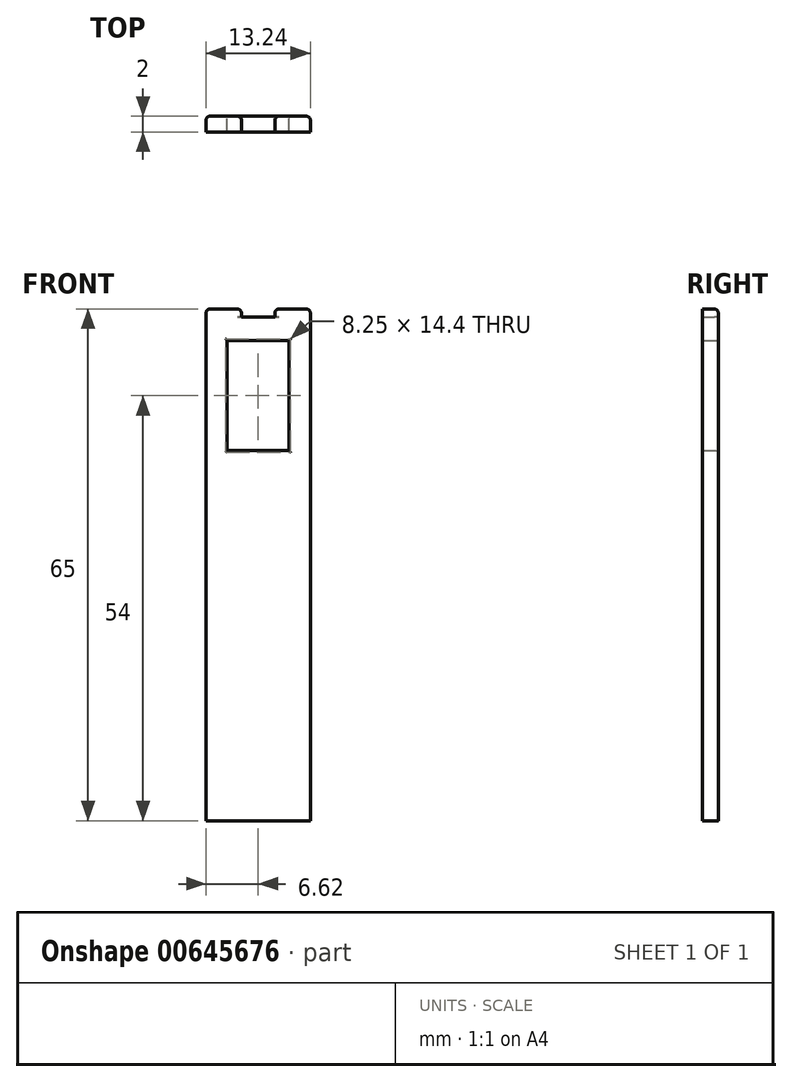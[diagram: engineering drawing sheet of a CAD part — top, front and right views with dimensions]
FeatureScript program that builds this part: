
annotation { "Feature Type Name" : "Feature", "Feature Type Description" : "" }
export const myFeature = defineFeature(function(context is Context, id is Id, definition is map)
    precondition{}
    {
        {
            var Q0;
            Q0=qCreatedBy(makeId("Front.planeOp"),FACE);
            var sketch = newSketch(context, id + "F0", { "sketchPlane" : qUnion([Q0])});
            skLineSegment(sketch, "E0.bottom", {"start": v(-6.62, 32.5) * mm, "end": v(6.63, 32.5) * mm});
            skLineSegment(sketch, "E0.top", {"start": v(-6.63, -32.5) * mm, "end": v(6.62, -32.5) * mm});
            skLineSegment(sketch, "E0.left", {"start": v(-6.62, 32.5) * mm, "end": v(-6.63, -32.5) * mm});
            skLineSegment(sketch, "E0.right", {"start": v(6.63, 32.5) * mm, "end": v(6.62, -32.5) * mm});
            skPoint(sketch, "E0.middle", {"position": v(0, 0) * mm});
            skLineSegment(sketch, "E1.bottom", {"start": v(-3.92, 28.5) * mm, "end": v(3.93, 28.5) * mm});
            skLineSegment(sketch, "E1.top", {"start": v(-3.92, 14.5) * mm, "end": v(3.93, 14.5) * mm});
            skLineSegment(sketch, "E1.left", {"start": v(-3.92, 28.5) * mm, "end": v(-3.92, 14.5) * mm});
            skLineSegment(sketch, "E1.right", {"start": v(3.93, 28.5) * mm, "end": v(3.93, 14.5) * mm});
            skSolve(sketch);
        }
        {
            var Q0;
            Q0=makeQuery(id+"F0.imprint","IMPRINT",FACE,{"disambiguationData":[TD([[makeQuery(id+"F0.imprint","IMPRINT",EDGE,{"derivedFrom":sQuery(id+"F0.wireOp",EDGE,"E0.bottom")}),-1.0]])]});
            extrude(context, id + "F1", {"entities" : qUnion([Q0]), "depth" : 2 * mm, "offsetDistance" : 25 * mm});
        }
        {
            var Q0;
            Q0=sQuery(id+"F0.wireOp",EDGE,"E1.left");
            var Q1;
            Q1=sQuery(id+"F0.wireOp",EDGE,"E1.bottom");
            var Q2;
            Q2=sQuery(id+"F0.wireOp",EDGE,"E1.right");
            var Q3;
            Q3=sQuery(id+"F0.wireOp",EDGE,"E1.top");
            extrude(context, id + "F2", {"bodyType" : ToolBodyType.SURFACE, "surfaceEntities" : qUnion([Q0, Q1, Q2, Q3]), "depth" : 2 * mm, "offsetDistance" : 25 * mm});
        }
        {
            var Q0;
            Q0=qCreatedBy(makeId("Front.planeOp"),FACE);
            var sketch = newSketch(context, id + "F3", { "sketchPlane" : qUnion([Q0])});
            skLineSegment(sketch, "E2.bottom", {"start": v(-2.13, 33.67) * mm, "end": v(2.12, 33.67) * mm});
            skLineSegment(sketch, "E2.top", {"start": v(-2.13, 31.5) * mm, "end": v(2.12, 31.5) * mm});
            skLineSegment(sketch, "E2.left", {"start": v(-2.13, 33.67) * mm, "end": v(-2.13, 31.5) * mm});
            skLineSegment(sketch, "E2.right", {"start": v(2.12, 33.67) * mm, "end": v(2.12, 31.5) * mm});
            skPoint(sketch, "E2.middle", {"position": v(0, 32.58) * mm});
            skSolve(sketch);
        }
        {
            var Q0;
            Q0=makeQuery(id+"F3.imprint","IMPRINT",FACE,{"disambiguationData":[TD([[makeQuery(id+"F3.imprint","IMPRINT",EDGE,{"derivedFrom":sQuery(id+"F3.wireOp",EDGE,"E2.bottom")}),-1.0]])]});
            extrude(context, id + "F4", {"entities" : qUnion([Q0]), "operationType" : NewBodyOperationType.REMOVE, "depth" : 25 * mm, "offsetDistance" : 25 * mm});
        }
        {
            var Q0;
            Q0=makeQuery(id+"F4.boolean.opBoolean","INTERSECT",EDGE,{"derivedFrom":[makeQuery(id+"F1.opExtrude","SWEPT_FACE",FACE,{"disambiguationData":[OSD([sQuery(id+"F0.wireOp",EDGE,"E0.bottom")])]}),makeQuery(id+"F4.opExtrude","SWEPT_FACE",FACE,{"disambiguationData":[OSD([sQuery(id+"F3.wireOp",EDGE,"E2.left")])]})]});
            var Q1;
            Q1=makeQuery(id+"F1.opExtrude","SWEPT_EDGE",EDGE,{"disambiguationData":[OSD([sQuery(id+"F0.wireOp",EDGE,"E0.bottom"),sQuery(id+"F0.wireOp",EDGE,"E0.left")])]});
            fillet(context, id + "F5", {"entities" : qUnion([Q0, Q1]), "radius" : 0.5 * mm, "tangentPropagation" : true, "allowEdgeOverflow" : false});
        }
        {
            var Q0;
            Q0=makeQuery(id+"F4.boolean.opBoolean","INTERSECT",EDGE,{"derivedFrom":[makeQuery(id+"F1.opExtrude","SWEPT_FACE",FACE,{"disambiguationData":[OSD([sQuery(id+"F0.wireOp",EDGE,"E0.bottom")])]}),makeQuery(id+"F4.opExtrude","SWEPT_FACE",FACE,{"disambiguationData":[OSD([sQuery(id+"F3.wireOp",EDGE,"E2.right")])]})]});
            var Q1;
            Q1=makeQuery(id+"F1.opExtrude","SWEPT_EDGE",EDGE,{"disambiguationData":[OSD([sQuery(id+"F0.wireOp",EDGE,"E0.bottom"),sQuery(id+"F0.wireOp",EDGE,"E0.right")])]});
            fillet(context, id + "F6", {"entities" : qUnion([Q0, Q1]), "radius" : 0.5 * mm, "tangentPropagation" : true, "allowEdgeOverflow" : false});
        }
        {
            var Q0;
            Q0=makeQuery(id+"F1.opExtrude","CAP_EDGE",EDGE,{"disambiguationData":[OSD([sQuery(id+"F0.wireOp",EDGE,"E1.left")])],"isStart":false});
            var Q1;
            Q1=makeQuery(id+"F1.opExtrude","CAP_EDGE",EDGE,{"disambiguationData":[OSD([sQuery(id+"F0.wireOp",EDGE,"E1.right")])],"isStart":false});
            var Q2;
            Q2=makeQuery(id+"F1.opExtrude","CAP_EDGE",EDGE,{"disambiguationData":[OSD([sQuery(id+"F0.wireOp",EDGE,"E1.right")])],"isStart":true});
            var Q3;
            Q3=makeQuery(id+"F1.opExtrude","CAP_EDGE",EDGE,{"disambiguationData":[OSD([sQuery(id+"F0.wireOp",EDGE,"E1.left")])],"isStart":true});
            var Q4;
            Q4=makeQuery(id+"F1.opExtrude","CAP_EDGE",EDGE,{"disambiguationData":[OSD([sQuery(id+"F0.wireOp",EDGE,"E1.bottom")])],"isStart":true});
            var Q5;
            Q5=makeQuery(id+"F1.opExtrude","CAP_EDGE",EDGE,{"disambiguationData":[OSD([sQuery(id+"F0.wireOp",EDGE,"E1.bottom")])],"isStart":false});
            var Q6;
            Q6=makeQuery(id+"F1.opExtrude","CAP_EDGE",EDGE,{"disambiguationData":[OSD([sQuery(id+"F0.wireOp",EDGE,"E1.top")])],"isStart":false});
            var Q7;
            Q7=makeQuery(id+"F1.opExtrude","CAP_EDGE",EDGE,{"disambiguationData":[OSD([sQuery(id+"F0.wireOp",EDGE,"E1.top")])],"isStart":true});
            fillet(context, id + "F7", {"entities" : qUnion([Q0, Q1, Q2, Q3, Q4, Q5, Q6, Q7]), "radius" : 0.2 * mm, "tangentPropagation" : true, "allowEdgeOverflow" : false});
        }
        {
            var Q0;
            Q0=makeQuery(id+"F1.opExtrude","CAP_EDGE",EDGE,{"disambiguationData":[OSD([sQuery(id+"F0.wireOp",EDGE,"E0.left")])],"isStart":true});
            var Q1;
            Q1=makeQuery(id+"F1.opExtrude","CAP_EDGE",EDGE,{"disambiguationData":[OSD([sQuery(id+"F0.wireOp",EDGE,"E0.right")])],"isStart":true});
            fillet(context, id + "F8", {"entities" : qUnion([Q0, Q1]), "radius" : 0.5 * mm, "tangentPropagation" : true, "allowEdgeOverflow" : false});
        }
    });
